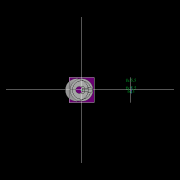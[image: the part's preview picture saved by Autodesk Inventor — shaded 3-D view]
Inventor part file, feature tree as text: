
AUTODESK INVENTOR PART (.ipt)
format: ipt  version: 2022.2 (Build 262287010, 287A)  size: 546,816 bytes
history: native  units: mm
features: other x20, extrude x19, sketch x13, pattern_circular x7, plane x5, fillet x2, move_body x2, revolve x2, draft x2, chamfer x2, loft x1
ambient origin geometry x8: Origin, YZ Plane, XZ Plane, XY Plane, X Axis, Y Axis, Z Axis, Center Point
bodies: Solid5 (feature_tree)
feature tree (75):
  other  "CrossSection1"
  sketch  "Sketch7"  dims[d90=15.767323mm]
  other  "Roller1"
  other  "Roller2"
  sketch  "Sketch22"  dims[d167=8.972256mm]
  sketch  "Sketch2"  dims[d57=4.025mm]
  sketch  "Sketch23"  dims[d173=10.814812mm]
  other  "RevRoller1"
  fillet  "Fillet1"  Radius=13.336791mm
  pattern_circular  "Circular Pattern13"  Count=360  [1 undecoded]
  move_body  "Move Body7"
  revolve  "Revolution13"  [1 undecoded]
  fillet  "Fillet3"  Radius=0.025mm
  pattern_circular  "Circular Pattern14"  [2 undecoded]
  move_body  "Move Body6"
  revolve  "Revolution14"  [1 undecoded]
  plane  "Work Plane7"
  sketch  "Sketch44"  dims[d349=17.374602mm]
  plane  "Work Plane8"
  loft  "Loft1"
  sketch  "Sketch46"  dims[d351=0.025mm]
  extrude  "Extrusion39"  Depth=5.5mm
  plane  "Work Plane9"
  sketch  "Sketch47"  dims[d352=0.025mm d354=0.025mm d355=17.374329mm d356=17.374602mm d357=1.0mm d358=90.0deg d359=0.5mm d360=60.0mm d361=360.0deg d363=30.0deg d367=8.1mm d369=4.014775mm d370=0.025mm d371=1.0mm d372=30.0deg d373=90.0deg d374=0.5mm d375=60.0mm d376=360.0deg d378=90.0deg d379=0.1mm d380=0.025mm d381=0.025mm d382=0.025mm d383=0.025mm d384=10.461905mm d385=0.0mm d386=0.0mm d391=1.0mm d392=53.5mm d393=1.5mm d394=1.5mm d395=1.5mm d396=1.5mm d397=90.0deg d398=90.0deg d399=90.0deg d400=53.5mm d401=10.461905mm d402=0.0mm d486=0.436332mm d487=0.5mm d488=2.0mm d489=0.0mm d490=20.0mm d495=2.5mm d496=8.0mm d506=13.856406mm d507=55.5mm d508=8.0mm d509=0.05mm d510=2.5mm d511=30.0deg d512=12.0mm d513=6.0mm d514=0.2mm d515=30.0deg d516=131.0mm d517=65.5mm d518=0.2mm d519=100.0mm d520=120.0mm d521=2.0mm d522=150.0mm d530=50.0mm d531=5.5mm d532=5.5mm d533=5.5mm d534=85.75mm d535=73.5mm d536=61.25mm d537=24.5mm d538=3.0mm d539=2.4mm d540=0.0mm d541=0.0mm d542=0.0mm d543=5.5mm d544=3.0mm d545=0.0mm d546=90.0mm d547=360.0deg d549=3.0mm d550=3.0mm d551=2.4mm d552=0.0mm d553=5.230953mm d554=0.0mm d555=2.4mm d556=0.0mm d557=5.230953mm d558=0.0mm d559=5.230953mm d560=0.0mm d561=90.0mm d562=360.0deg d564=60.0mm d565=360.0deg d567=5.5mm d568=5.5mm d569=3.0mm d570=0.0mm d571=5.230953mm d572=0.0mm d573=3.0mm d574=0.0mm d575=5.230953mm d576=0.0mm d577=90.0mm d578=360.0deg d580=60.0mm d581=360.0deg d584=20.0mm d585=8.0mm d587=1.75mm d589=3.0mm d592=2.0mm d593=12.0mm d594=12.0mm d600=0.5mm d601=2.0mm d602=45.0deg d603=0.5mm d604=2.0mm d605=45.0deg d606=0.436332mm d607=0.5mm d608=0.0mm d609=20.0mm d611=360.0deg d613=0.0mm d614=0.0mm d615=20.0mm d616=3.376mm d617=0.0mm d618=90.0deg d619=0.0mm d620=90.0deg d621=2.5mm d622=7.0mm d623=0.0mm d624=0.0mm d625=50.0mm d626=5.5mm d627=3.0mm d628=5.5mm d629=43.459mm d630=0.0mm d631=52.538mm d632=0.0mm d633=4.8mm d634=0.0mm d16=0.872665mm d17=0.872665mm d49=0.872665mm d50=0.872665mm d51=0.872665mm d52=0.872665mm d236=0.5mm d237=0.872665mm d238=0.5mm d239=0.872665mm d282=1.0mm d283=1.0mm d284=1.0mm d285=0.15mm d286=0.25mm d287=0.375mm d288=14.3117mm d289=0.75mm d290=20.594885mm d291=0.0625mm d292=0.75mm d293=0.375mm d405=0.5mm d406=0.872665mm d407=0.5mm d408=0.872665mm d413=0.5mm d414=0.872665mm d415=0.5mm d416=0.872665mm d417=0.5mm d418=0.872665mm d419=0.5mm d420=0.872665mm d421=0.872665mm d431=0.5mm d432=0.872665mm d433=0.5mm d434=0.872665mm d471=0.5mm d472=0.872665mm d473=0.5mm d474=0.872665mm d497=0.5mm d498=0.872665mm d499=0.5mm d500=0.872665mm d590=0.5mm d591=0.872665mm]
  extrude  "Extrusion40"  TaperAngle=90.0deg  [1 undecoded]
  extrude  "Extrusion41"  Depth=5.5mm
  extrude  "Extrusion42"  Depth=5.5mm
  other  "OuterRim_Top2"
  other  "OuterRim_Bottom2"
  extrude  "Rotor_Ring"  TaperAngle=360.0deg  [1 undecoded]
  draft  "FaceDraft2"
  sketch  "Sketch30"  dims[d201=53.5mm d232=0.0mm d233=3600.0mm]
  plane  "Work Plane5"
  other  "Rotor Featurs"
  other  "RotorRim_Bottom"
  extrude  "Extrusion24"  TaperAngle=30.0deg  [1 undecoded]
  extrude  "Extrusion25"  Depth=5.5mm
  extrude  "Extrusion26"  Depth=5.5mm
  pattern_circular  "Circular Pattern23"  [2 undecoded]
  sketch  "Sketch41"  dims[d346=0.025mm]
  extrude  "Extrusion27"  Depth=5.5mm
  extrude  "Extrusion28"  TaperAngle=30.0deg  [1 undecoded]
  pattern_circular  "Circular Pattern24"  Angle=90.0deg  [1 undecoded]
  extrude  "Extrusion29"  Depth=5.5mm
  extrude  "Extrusion30"  Depth=5.5mm
  extrude  "Extrusion31"  TaperAngle=360.0deg  [1 undecoded]
  pattern_circular  "Circular Pattern25"  Angle=90.0deg  [1 undecoded]
  sketch  "Sketch42"  dims[d347=0.1mm]
  extrude  "Extrusion32"  Depth=0.1mm
  extrude  "Extrusion33"  Depth=5.5mm
  extrude  "Extrusion34"  Depth=5.5mm
  extrude  "Extrusion35"  Depth=5.5mm
  pattern_circular  "Circular Pattern26"  [2 undecoded]
  pattern_circular  "Circular Pattern27"  [2 undecoded]
  chamfer  "Chamfer1"  [1 undecoded]
  chamfer  "Chamfer2"  [1 undecoded]
  draft  "FaceDraft4"
  plane  "Work Plane6"
  sketch  "Sketch43"  dims[d348=0.1mm]
  extrude  "Extrusion37"  Depth=5.5mm
  extrude  "Extrusion38"  Depth=5.5mm
  other  "2D Equation Curve1"
  sketch  "Sketch40"  dims[d343=17.374329mm d344=17.374602mm d345=0.025mm]
  other  "Work Axis6"
  other  "Work Axis7"
  other  "Work Axis8"
  other  "Work Axis9"
  other  "Work Axis10"
  other  "Work Point1"
  other  "Work Point2"
  other  "Work Point3"
  other  "Work Point4"
  other  "Work Point5"
  sketch  "Sketch45"  dims[d350=17.374329mm]
  other  "Edges1"
note: 20 required parameter values undecoded (feature->parameter linkage not recoverable at this tier; creation-order binding heuristic only, values carry confidence <= 0.55)